SOLIDWORKS PART (.sldprt)
format: sldprt  version: not decoded by parser v0  size: 6,223,360 bytes
history: native  units: mm
features: sketch x5, plane x3, sweep x2, material x1, helix x1, pattern_linear x1 (+8 scaffold rows collapsed)
feature tree (21):
  scaffold x8  (default folders/planes/origin — collapsed)
  material  "Kupfer"
  plane  "Ebene vorne"
  plane  "Ebene oben"
  plane  "Ebene rechts"
  sketch  "Skizze1"  dims[D1=500.0mm]
  helix  "Spirale/Helix1"  Pitch=1000mm
  sketch  "Skizze2"  dims[D1=19.0mm D2=22.0mm]
  sweep  "Austragung1"
  sketch  "Skizze3"  dims[D4=500.0mm D1=5.0mm D2=25.0mm D3=261.0mm]
  sketch  "Skizze4"  dims[D1=500.0mm Spirale/Helix2=0.0 D3=200.0mm D4=100.0mm D5=2000.0mm D7=90.0deg]
  sweep  "Austragung2"
  sketch  "Skizze5"
  pattern_linear  "Lineares Muster1"  Count1=5 Count2=1 Spacing1=200mm Spacing2=10mm
decode coverage: 6 of 9 modeling features carry decoded parameters
note: suppression state not decoded; provenance and decode notes live in map.json
